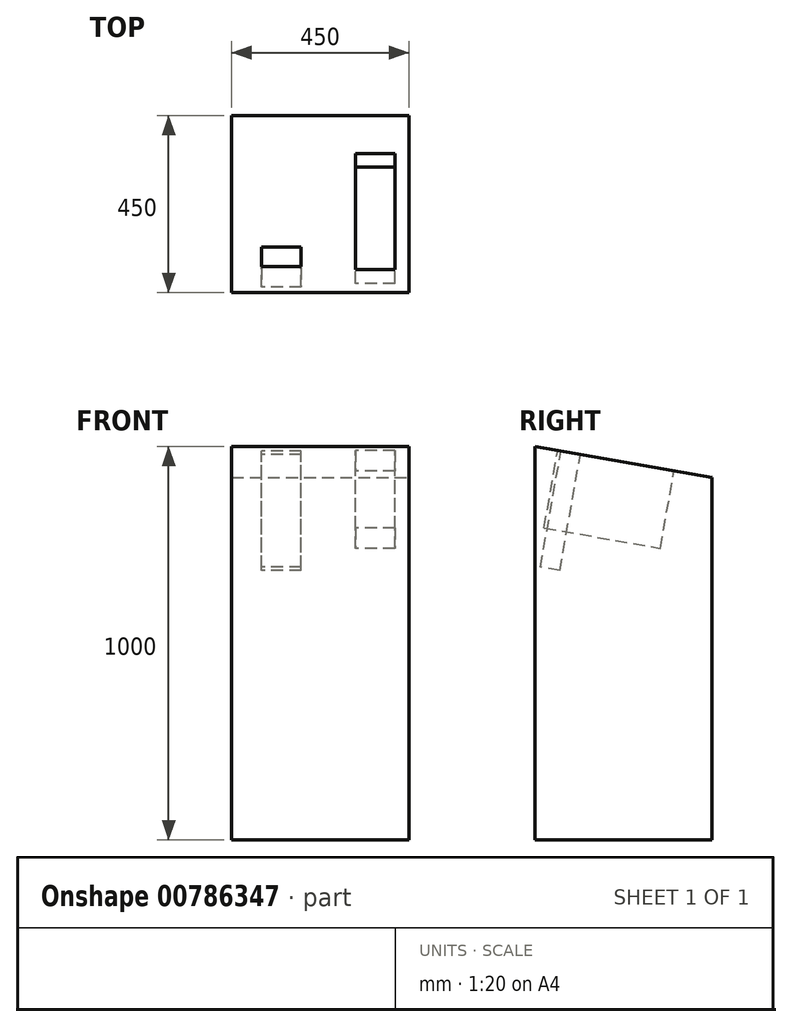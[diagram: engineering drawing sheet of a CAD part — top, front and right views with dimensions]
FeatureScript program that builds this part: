
annotation { "Feature Type Name" : "Feature", "Feature Type Description" : "" }
export const myFeature = defineFeature(function(context is Context, id is Id, definition is map)
    precondition{}
    {
        {
            var Q0;
            Q0=qCreatedBy(makeId("Right.planeOp"),FACE);
            var sketch = newSketch(context, id + "F0", { "sketchPlane" : qUnion([Q0])});
            skLineSegment(sketch, "E0.bottom", {"start": v(-225, 500) * mm, "end": v(225, 500) * mm});
            skLineSegment(sketch, "E0.top", {"start": v(-225, -500) * mm, "end": v(225, -500) * mm});
            skLineSegment(sketch, "E0.left", {"start": v(-225, 500) * mm, "end": v(-225, -500) * mm});
            skLineSegment(sketch, "E0.right", {"start": v(225, 500) * mm, "end": v(225, -500) * mm});
            skPoint(sketch, "E0.middle", {"position": v(0, 0) * mm});
            skSolve(sketch);
        }
        {
            var Q0;
            Q0 = qSketchRegion(id + "F0", true);
            extrude(context, id + "F1", {"entities" : qUnion([Q0]), "depth" : 450 * mm, "offsetDistance" : 25 * mm});
        }
        {
            var Q0;
            Q0=makeQuery(id+"F1.opExtrude","SWEPT_EDGE",EDGE,{"disambiguationData":[OSD([sQuery(id+"F0.wireOp",EDGE,"E0.bottom"),sQuery(id+"F0.wireOp",EDGE,"E0.right")])]});
            chamfer(context, id + "F2", {"entities" : qUnion([Q0]), "chamferType" : ChamferType.OFFSET_ANGLE, "width" : 450 * mm, "oppositeDirection" : false, "angle" : 10 * degree, "tangentPropagation" : true});
        }
        {
            var Q0;
            Q0=makeQuery(id+"F2.opChamfer","BLEND_FACE",FACE,{"disambiguationData":[OSD([sQuery(id+"F0.wireOp",EDGE,"E0.bottom"),sQuery(id+"F0.wireOp",EDGE,"E0.right")])]});
            var sketch = newSketch(context, id + "F3", { "sketchPlane" : qUnion([Q0])});
            skLineSegment(sketch, "E1.bottom", {"start": v(414.6, -249.07) * mm, "end": v(314.6, -249.07) * mm});
            skLineSegment(sketch, "E1.top", {"start": v(414.6, 50.93) * mm, "end": v(314.6, 50.93) * mm});
            skLineSegment(sketch, "E1.left", {"start": v(414.6, -249.07) * mm, "end": v(414.6, 50.93) * mm});
            skLineSegment(sketch, "E1.right", {"start": v(314.6, -249.07) * mm, "end": v(314.6, 50.93) * mm});
            skPoint(sketch, "E1.middle", {"position": v(364.6, -99.07) * mm});
            skLineSegment(sketch, "E2.bottom", {"start": v(176.4, -190.78) * mm, "end": v(76.4, -190.78) * mm});
            skLineSegment(sketch, "E2.top", {"start": v(176.4, -240.78) * mm, "end": v(76.4, -240.78) * mm});
            skLineSegment(sketch, "E2.left", {"start": v(176.4, -190.78) * mm, "end": v(176.4, -240.78) * mm});
            skLineSegment(sketch, "E2.right", {"start": v(76.4, -190.78) * mm, "end": v(76.4, -240.78) * mm});
            skPoint(sketch, "E2.middle", {"position": v(126.4, -215.78) * mm});
            skSolve(sketch);
        }
        {
            var Q0;
            Q0=makeQuery(id+"F3.imprint","IMPRINT",FACE,{"disambiguationData":[TD([[makeQuery(id+"F3.imprint","IMPRINT",EDGE,{"derivedFrom":sQuery(id+"F3.wireOp",EDGE,"E1.bottom")}),-1.0]])]});
            extrude(context, id + "F4", {"entities" : qUnion([Q0]), "operationType" : NewBodyOperationType.REMOVE, "oppositeDirection" : true, "depth" : 200 * mm, "offsetDistance" : 25 * mm});
        }
        {
            var Q0;
            Q0=makeQuery(id+"F3.imprint","IMPRINT",FACE,{"disambiguationData":[TD([[makeQuery(id+"F3.imprint","IMPRINT",EDGE,{"derivedFrom":sQuery(id+"F3.wireOp",EDGE,"E2.bottom")}),1.0]])]});
            extrude(context, id + "F5", {"entities" : qUnion([Q0]), "operationType" : NewBodyOperationType.REMOVE, "oppositeDirection" : true, "depth" : 300 * mm, "offsetDistance" : 25 * mm});
        }
    });
